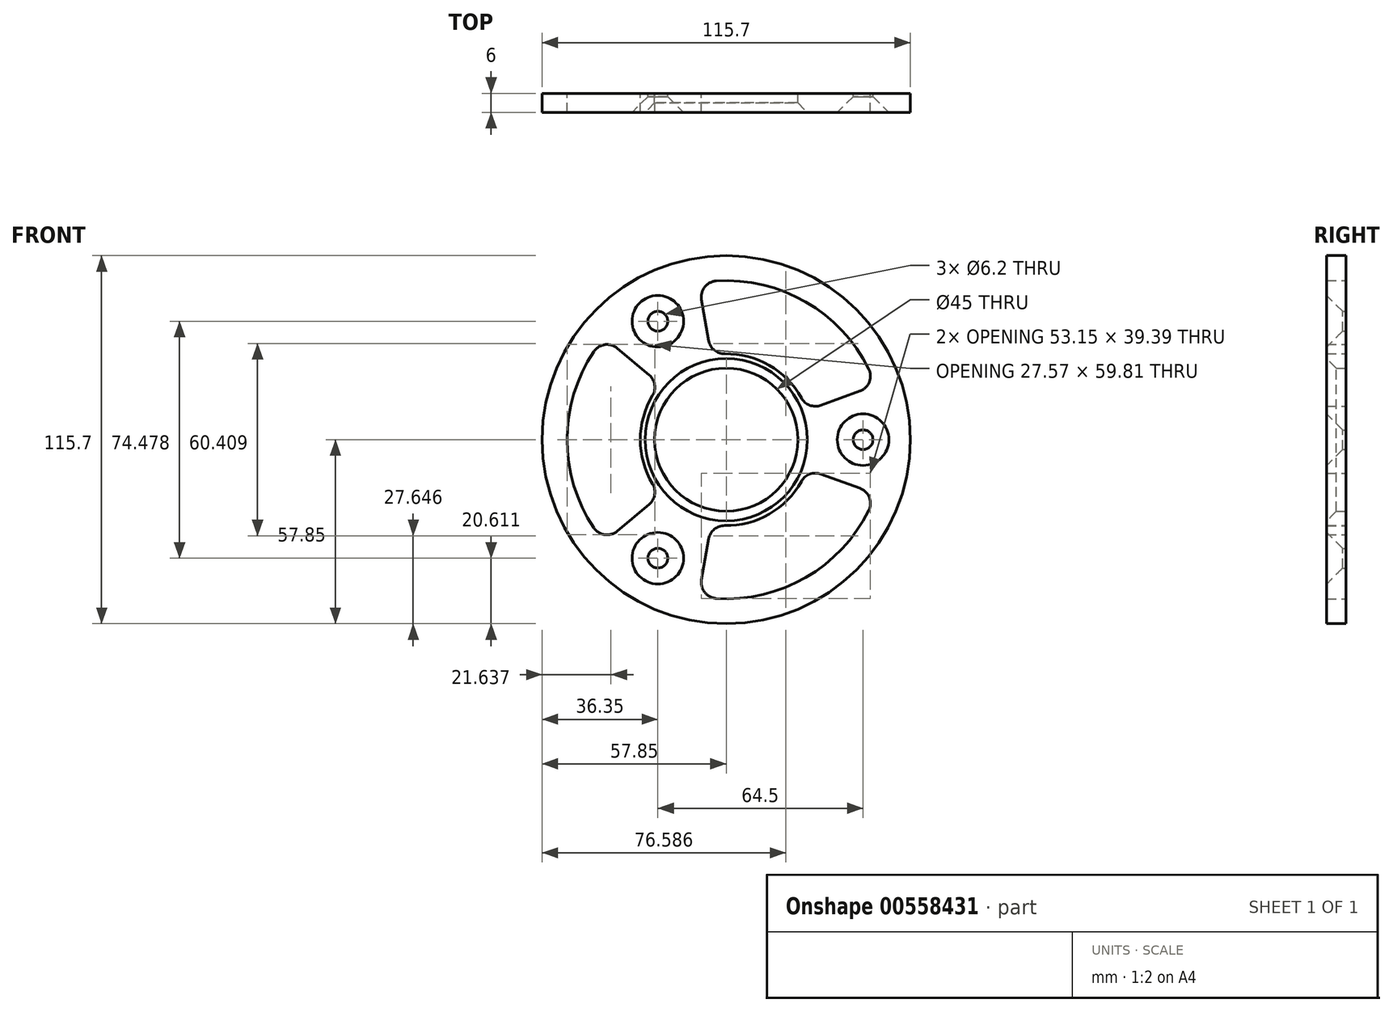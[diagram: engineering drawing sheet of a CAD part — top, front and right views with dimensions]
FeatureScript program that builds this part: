
annotation { "Feature Type Name" : "Feature", "Feature Type Description" : "" }
export const myFeature = defineFeature(function(context is Context, id is Id, definition is map)
    precondition{}
    {
        {
            var Q0;
            Q0=qCreatedBy(makeId("Front.planeOp"),FACE);
            var sketch = newSketch(context, id + "F0", { "sketchPlane" : qUnion([Q0])});
            skCircle(sketch, "E0", {"center": v(0, 0) * mm, "radius": 57.85 * mm});
            skCircle(sketch, "E1", {"center": v(0, 0) * mm, "radius": 22.5 * mm});
            skArc(sketch, "E2", {"start": v(-25.2, 9.68) * mm, "mid": v(-27, 0) * mm, "end": v(-25.2, -9.68) * mm});
            skArc(sketch, "E3", {"start": v(-45.81, 20.03) * mm, "mid": v(-50, 0) * mm, "end": v(-45.81, -20.03) * mm});
            skPoint(sketch, "E4.visualSharp", {"position": v(-23.38, 13.5) * mm});
            skPoint(sketch, "E5.visualSharp", {"position": v(-43.3, 25) * mm});
            skPoint(sketch, "E6.visualSharp", {"position": v(-43.3, -25) * mm});
            skPoint(sketch, "E7.visualSharp", {"position": v(-23.38, -13.5) * mm});
            skPoint(sketch, "E8.MirrorP", {"position": v(23.38, -13.5) * mm});
            skPoint(sketch, "E9.MirrorP", {"position": v(0, -50) * mm});
            skPoint(sketch, "E10.MirrorP", {"position": v(0, -27) * mm});
            skArc(sketch, "E11.MirrorCS", {"start": v(20.99, -16.99) * mm, "mid": v(13.5, -23.38) * mm, "end": v(4.22, -26.67) * mm});
            skArc(sketch, "E12.MirrorCS", {"start": v(40.26, -29.66) * mm, "mid": v(25, -43.3) * mm, "end": v(5.56, -49.7) * mm});
            skArc(sketch, "E13.MirrorCS", {"start": v(4.22, 26.67) * mm, "mid": v(13.5, 23.38) * mm, "end": v(20.99, 16.99) * mm});
            skArc(sketch, "E14.MirrorCS", {"start": v(5.56, 49.7) * mm, "mid": v(25, 43.3) * mm, "end": v(40.26, 29.66) * mm});
            skPoint(sketch, "E15.MirrorP", {"position": v(0, 50) * mm});
            skPoint(sketch, "E16.MirrorP", {"position": v(43.3, 25) * mm});
            skCircle(sketch, "E17", {"center": v(43, 0) * mm, "radius": 3.1 * mm});
            skCircle(sketch, "E18.MirrorC", {"center": v(-21.5, 37.24) * mm, "radius": 3.1 * mm});
            skCircle(sketch, "E19.MirrorC", {"center": v(-21.5, -37.24) * mm, "radius": 3.1 * mm});
            skArc(sketch, "E20", {"start": v(20.99, 16.99) * mm, "mid": v(11.41, 24.47) * mm, "end": v(-0.48, 27) * mm});
            skArc(sketch, "E21", {"start": v(-45.81, 20.03) * mm, "mid": v(-49.92, -2.78) * mm, "end": v(-43.3, -25) * mm});
            skArc(sketch, "E22.trimOffspring", {"start": v(0, -50) * mm, "mid": v(22.55, -44.63) * mm, "end": v(40.26, -29.66) * mm});
            skArc(sketch, "E23.trimOffspring", {"start": v(40.26, 29.66) * mm, "mid": v(21.13, 45.32) * mm, "end": v(-3.16, 49.9) * mm});
            skLineSegment(sketch, "E24.trimOffspring", {"start": v(-10.05, 56.97) * mm, "end": v(-12, 68.06) * mm});
            skLineSegment(sketch, "E25.trimOffspring", {"start": v(-5.49, 31.13) * mm, "end": v(-7.77, 44.04) * mm});
            skLineSegment(sketch, "E26", {"start": v(-24.21, 20.32) * mm, "end": v(-34.26, 28.75) * mm});
            skArc(sketch, "E27", {"start": v(0, -27) * mm, "mid": v(13.5, -23.38) * mm, "end": v(23.38, -13.5) * mm});
            skArc(sketch, "E28.trimOffspring", {"start": v(40.26, 29.66) * mm, "mid": v(18.58, 46.42) * mm, "end": v(-8.68, 49.24) * mm});
            skArc(sketch, "E29.trimOffspring", {"start": v(-23.14, 13.91) * mm, "mid": v(-27, 0.24) * mm, "end": v(-23.38, -13.5) * mm});
            skArc(sketch, "E30.trimOffspring", {"start": v(-41.64, 27.68) * mm, "mid": v(-49.98, 1.58) * mm, "end": v(-43.3, -25) * mm});
            skArc(sketch, "E31.MirrorCS", {"start": v(-41.64, -27.68) * mm, "mid": v(-49.98, -1.58) * mm, "end": v(-43.3, 25) * mm});
            skArc(sketch, "E32.MirrorCS", {"start": v(-23.14, -13.91) * mm, "mid": v(-27, -0.24) * mm, "end": v(-23.38, 13.5) * mm});
            skLineSegment(sketch, "E33.MirrorCS", {"start": v(-24.21, -20.32) * mm, "end": v(-34.26, -28.75) * mm});
            skArc(sketch, "E34.MirrorCS", {"start": v(5.56, 49.7) * mm, "mid": v(28.68, 40.96) * mm, "end": v(44.8, 22.22) * mm});
            skLineSegment(sketch, "E35.MirrorCS", {"start": v(29.7, 10.81) * mm, "end": v(42.02, 15.3) * mm});
            skArc(sketch, "E36.MirrorCS", {"start": v(20.99, 16.99) * mm, "mid": v(13.5, 23.38) * mm, "end": v(4.22, 26.67) * mm});
            skArc(sketch, "E37.MirrorCS", {"start": v(4.22, 26.67) * mm, "mid": v(15.49, 22.12) * mm, "end": v(23.62, 13.09) * mm});
            skLineSegment(sketch, "E38", {"start": v(0, 0) * mm, "end": v(119.14, 0) * mm});
            skLineSegment(sketch, "E39.MirrorCS", {"start": v(29.7, -10.81) * mm, "end": v(42.02, -15.3) * mm});
            skArc(sketch, "E40.MirrorCS", {"start": v(4.22, -26.67) * mm, "mid": v(15.49, -22.12) * mm, "end": v(23.62, -13.09) * mm});
            skArc(sketch, "E41.MirrorCS", {"start": v(5.56, -49.7) * mm, "mid": v(28.68, -40.96) * mm, "end": v(44.8, -22.22) * mm});
            skLineSegment(sketch, "E42.MirrorCS", {"start": v(-5.49, -31.13) * mm, "end": v(-7.77, -44.04) * mm});
            skArc(sketch, "E43.MirrorCS", {"start": v(-3.16, -49.9) * mm, "mid": v(23.62, -44.07) * mm, "end": v(43.3, -25) * mm});
            skArc(sketch, "E44.MirrorCS", {"start": v(-0.48, -27) * mm, "mid": v(13.3, -23.5) * mm, "end": v(23.38, -13.5) * mm});
            skPoint(sketch, "E45.visualSharp", {"position": v(-38.3, -32.14) * mm});
            skArc(sketch, "E45.filletArc", {"start": v(-41.64, -27.68) * mm, "mid": v(-38.18, -29.87) * mm, "end": v(-34.26, -28.75) * mm});
            skPoint(sketch, "E46.visualSharp", {"position": v(-38.3, 32.14) * mm});
            skArc(sketch, "E46.filletArc", {"start": v(-34.26, 28.75) * mm, "mid": v(-38.18, 29.87) * mm, "end": v(-41.64, 27.68) * mm});
            skPoint(sketch, "E47.visualSharp", {"position": v(-20.68, 17.36) * mm});
            skArc(sketch, "E47.filletArc", {"start": v(-23.14, 13.91) * mm, "mid": v(-22.5, 17.31) * mm, "end": v(-24.21, 20.32) * mm});
            skPoint(sketch, "E48.visualSharp", {"position": v(-20.68, -17.36) * mm});
            skArc(sketch, "E48.filletArc", {"start": v(-24.21, -20.32) * mm, "mid": v(-22.5, -17.31) * mm, "end": v(-23.14, -13.91) * mm});
            skPoint(sketch, "E49.visualSharp", {"position": v(-4.69, -26.59) * mm});
            skArc(sketch, "E49.filletArc", {"start": v(-0.48, -27) * mm, "mid": v(-3.74, -28.14) * mm, "end": v(-5.49, -31.13) * mm});
            skPoint(sketch, "E50.visualSharp", {"position": v(-8.68, -49.24) * mm});
            skArc(sketch, "E50.filletArc", {"start": v(-7.77, -44.04) * mm, "mid": v(-6.77, -48) * mm, "end": v(-3.16, -49.9) * mm});
            skPoint(sketch, "E51.visualSharp", {"position": v(46.98, -17.1) * mm});
            skArc(sketch, "E51.filletArc", {"start": v(44.8, -22.22) * mm, "mid": v(44.96, -18.14) * mm, "end": v(42.02, -15.3) * mm});
            skPoint(sketch, "E52.visualSharp", {"position": v(25.37, -9.23) * mm});
            skArc(sketch, "E52.filletArc", {"start": v(29.7, -10.81) * mm, "mid": v(26.24, -10.83) * mm, "end": v(23.62, -13.09) * mm});
            skPoint(sketch, "E53.visualSharp", {"position": v(46.98, 17.1) * mm});
            skArc(sketch, "E53.filletArc", {"start": v(42.02, 15.3) * mm, "mid": v(44.96, 18.14) * mm, "end": v(44.8, 22.22) * mm});
            skPoint(sketch, "E54.visualSharp", {"position": v(25.37, 9.23) * mm});
            skArc(sketch, "E54.filletArc", {"start": v(23.62, 13.09) * mm, "mid": v(26.24, 10.83) * mm, "end": v(29.7, 10.81) * mm});
            skPoint(sketch, "E55.visualSharp", {"position": v(-4.69, 26.59) * mm});
            skArc(sketch, "E55.filletArc", {"start": v(-5.49, 31.13) * mm, "mid": v(-3.74, 28.14) * mm, "end": v(-0.48, 27) * mm});
            skPoint(sketch, "E56.visualSharp", {"position": v(-8.68, 49.24) * mm});
            skArc(sketch, "E56.filletArc", {"start": v(-3.16, 49.9) * mm, "mid": v(-6.77, 48) * mm, "end": v(-7.77, 44.04) * mm});
            skSolve(sketch);
        }
        {
            var Q0;
            Q0=makeQuery(id+"F0.imprint","IMPRINT",FACE,{"disambiguationData":[TD([[makeQuery(id+"F0.imprint","IMPRINT",EDGE,{"derivedFrom":sQuery(id+"F0.wireOp",EDGE,"E0")}),1.0]])]});
            extrude(context, id + "F1", {"entities" : qUnion([Q0]), "depth" : 6 * mm, "offsetDistance" : 25 * mm});
        }
        {
            var Q0;
            Q0=makeQuery(id+"F1.opExtrude","CAP_EDGE",EDGE,{"disambiguationData":[OSD([sQuery(id+"F0.wireOp",EDGE,"E1")])],"isStart":false});
            chamfer(context, id + "F2", {"entities" : qUnion([Q0]), "chamferType" : ChamferType.TWO_OFFSETS, "width1" : 3 * mm, "oppositeDirection" : false, "width2" : 3 * mm, "tangentPropagation" : true});
        }
        {
            var Q0;
            Q0=makeQuery(id+"F1.opExtrude","CAP_EDGE",EDGE,{"disambiguationData":[OSD([sQuery(id+"F0.wireOp",EDGE,"E18.MirrorC")])],"isStart":false});
            chamfer(context, id + "F3", {"entities" : qUnion([Q0]), "chamferType" : ChamferType.OFFSET_ANGLE, "width" : 5 * mm, "oppositeDirection" : false, "angle" : 45 * degree, "tangentPropagation" : true});
        }
        {
            var Q0;
            Q0=makeQuery(id+"F1.opExtrude","CAP_EDGE",EDGE,{"disambiguationData":[OSD([sQuery(id+"F0.wireOp",EDGE,"E19.MirrorC")])],"isStart":false});
            chamfer(context, id + "F4", {"entities" : qUnion([Q0]), "width" : 5 * mm, "tangentPropagation" : true});
        }
        {
            var Q0;
            Q0=makeQuery(id+"F1.opExtrude","CAP_EDGE",EDGE,{"disambiguationData":[OSD([sQuery(id+"F0.wireOp",EDGE,"E17")])],"isStart":false});
            chamfer(context, id + "F5", {"entities" : qUnion([Q0]), "chamferType" : ChamferType.OFFSET_ANGLE, "width" : 5 * mm, "oppositeDirection" : false, "angle" : 45 * degree, "tangentPropagation" : true});
        }
    });
